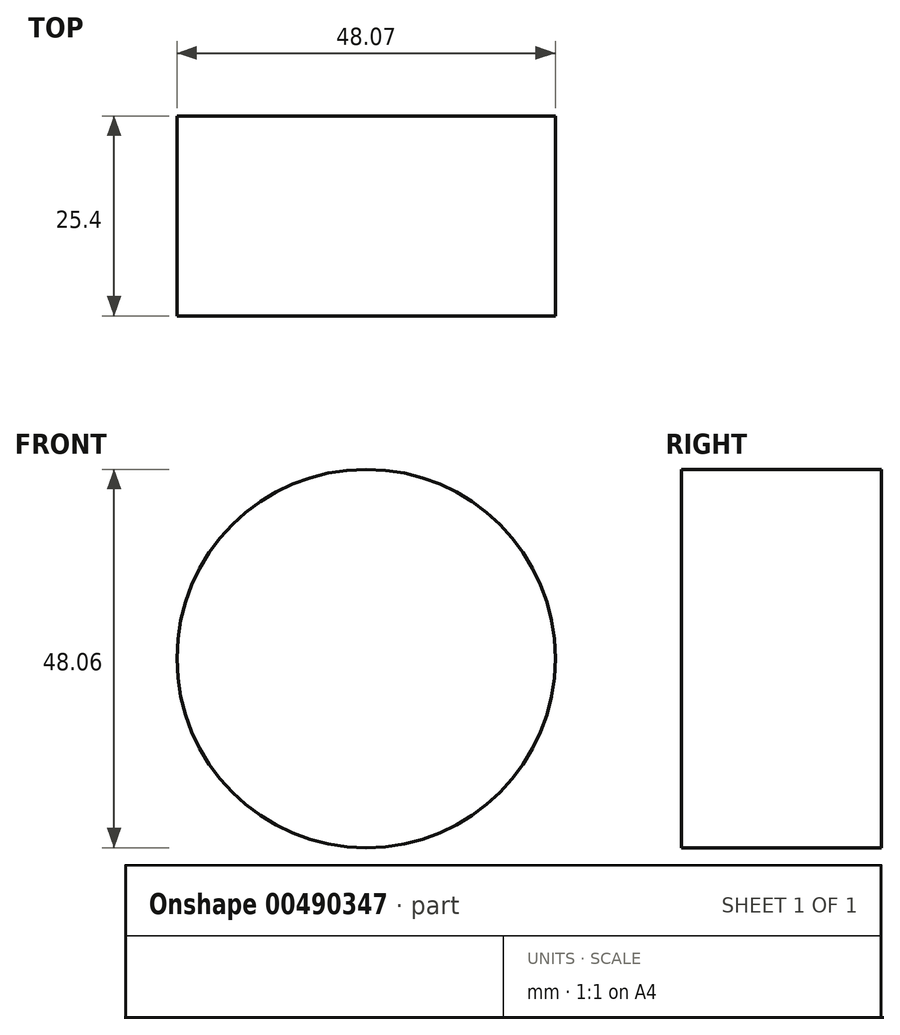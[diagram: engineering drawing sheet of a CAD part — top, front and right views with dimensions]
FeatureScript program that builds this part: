
annotation { "Feature Type Name" : "Feature", "Feature Type Description" : "" }
export const myFeature = defineFeature(function(context is Context, id is Id, definition is map)
    precondition{}
    {
        {
            var Q0;
            Q0=qCreatedBy(makeId("Front.planeOp"),FACE);
            var sketch = newSketch(context, id + "F0", { "sketchPlane" : qUnion([Q0])});
            skArc(sketch, "E0", {"start": v(54.27, 16.23) * mm, "mid": v(-0.04, 48.03) * mm, "end": v(-58.47, 24.62) * mm});
            skCircle(sketch, "E1", {"center": v(-27.14, 0) * mm, "radius": 24.03 * mm});
            skSolve(sketch);
        }
        {
            var Q0;
            Q0 = qSketchRegion(id + "F0", true);
            extrude(context, id + "F1", {"entities" : qUnion([Q0]), "depth" : 25.4 * mm});
        }
    });
